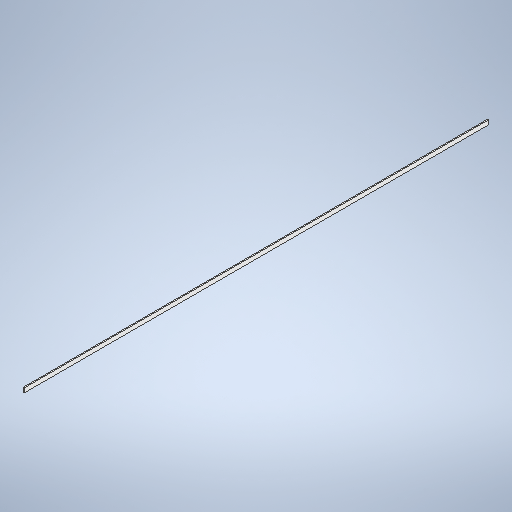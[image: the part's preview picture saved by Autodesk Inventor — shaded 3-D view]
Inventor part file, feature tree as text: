
AUTODESK INVENTOR PART (.ipt)
format: ipt  version: 2025.1 (Build 291241020, 241B)  size: 256,000 bytes
history: native  units: in
note: dims shown in document units (in); Inventor stores cm internally (conversion verified against a paired STEP export)
features: extrude x1, sketch x1
ambient origin geometry x8: Origin, YZ Plane, XZ Plane, XY Plane, X Axis, Y Axis, Z Axis, Center Point
bodies: Solid1 (feature_tree)
feature tree (2):
  extrude  "Extrusion1"  Depth=0.3125in TaperAngle=0.0deg
  sketch  "Sketch1"  dims[d1=1.25in d2=0.3125in d3=0.0in d4=135.013in]
